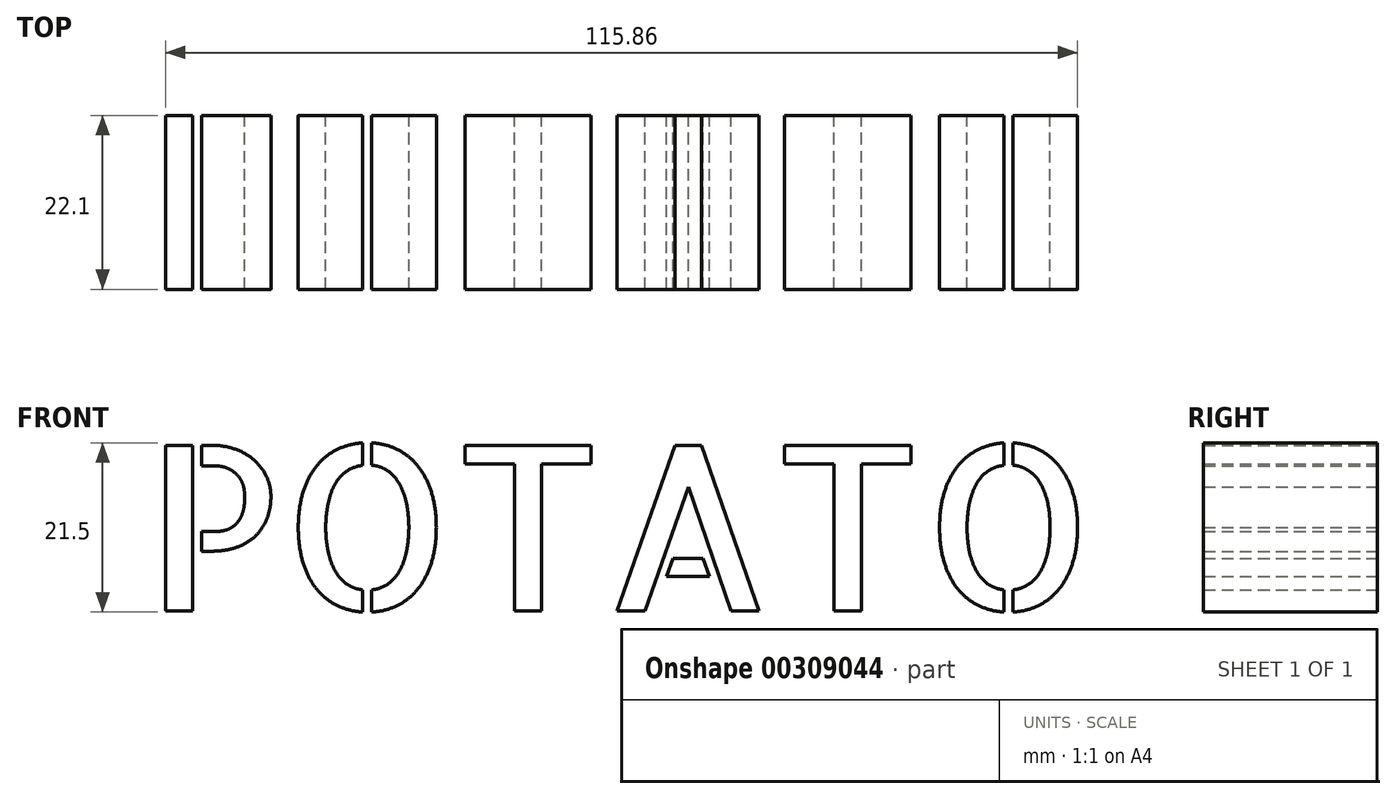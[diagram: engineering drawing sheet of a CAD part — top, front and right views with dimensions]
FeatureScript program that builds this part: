
annotation { "Feature Type Name" : "Feature", "Feature Type Description" : "" }
export const myFeature = defineFeature(function(context is Context, id is Id, definition is map)
    precondition{}
    {
        {
            var Q0;
            Q0=qCreatedBy(makeId("Front.planeOp"),FACE);
            var sketch = newSketch(context, id + "F0", { "sketchPlane" : qUnion([Q0])});
            skText(sketch, "E0", { "text": "POTATO", "fontName": "AllertaStencil-Regular.ttf"});
            const initialGuessF0  = {"E0": [-0.04418, 0.01024, 1, 0, 0.02105]};
            skSetInitialGuess(sketch, initialGuessF0);
            skSolve(sketch);
        }
        {
            var Q0;
            Q0=makeQuery(id+"F0.imprint","IMPRINT",FACE,{"disambiguationData":[TD([[makeQuery(id+"F0.imprint","IMPRINT",EDGE,{"derivedFrom":sQuery(id+"F0.wireOp",EDGE,"E0.sketch_text.stroke-0")}),-1.0]])]});
            var Q1;
            Q1 = qSketchRegion(id + "F0", true);
            extrude(context, id + "F1", {"entities" : qUnion([Q0, Q1]), "depth" : 22.1 * mm});
        }
    });
